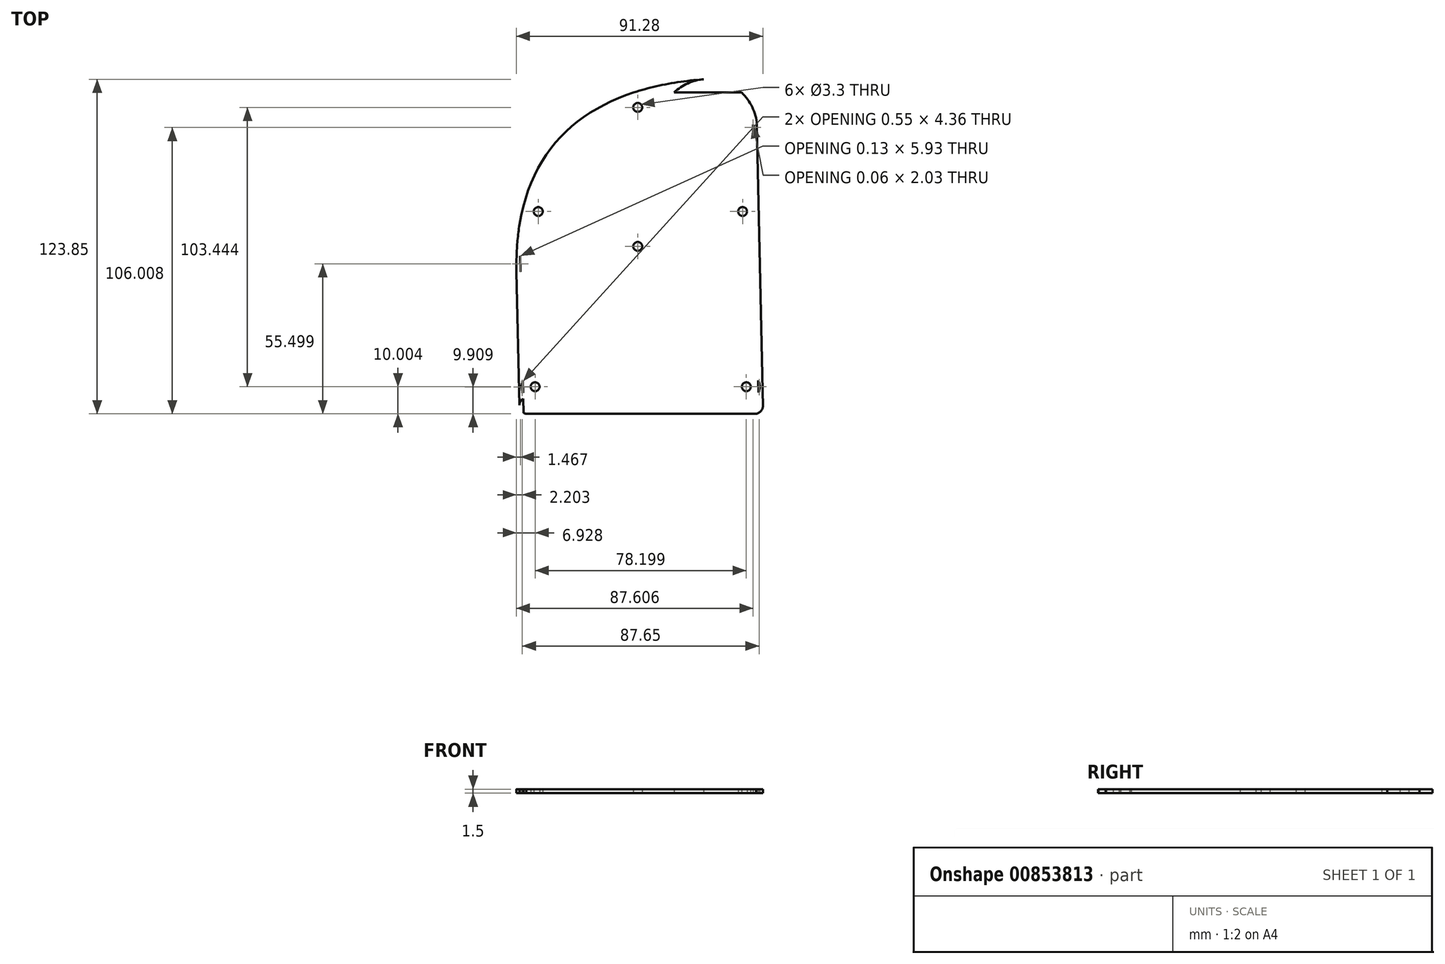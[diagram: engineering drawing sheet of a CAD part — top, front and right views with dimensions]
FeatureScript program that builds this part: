
annotation { "Feature Type Name" : "Feature", "Feature Type Description" : "" }
export const myFeature = defineFeature(function(context is Context, id is Id, definition is map)
    precondition{}
    {
        {
            var Q0;
            Q0=qCreatedBy(makeId("Top.planeOp"),FACE);
            var sketch = newSketch(context, id + "F0", { "sketchPlane" : qUnion([Q0])});
            skLineSegment(sketch, "E0.bottom", {"start": v(-43.8, -61.99) * mm, "end": v(46.4, -61.99) * mm});
            skLineSegment(sketch, "E0.top", {"start": v(-46.4, 61.99) * mm, "end": v(43.8, 61.99) * mm});
            skLineSegment(sketch, "E0.left", {"start": v(-43.8, -61.99) * mm, "end": v(-46.4, 61.99) * mm});
            skLineSegment(sketch, "E0.right", {"start": v(46.4, -61.99) * mm, "end": v(43.8, 61.99) * mm});
            skPoint(sketch, "E0.middle", {"position": v(0, 0) * mm});
            skCircle(sketch, "E1", {"center": v(25.95, 43.67) * mm, "radius": 16.76 * mm});
            skLineSegment(sketch, "E2", {"start": v(26.25, -9.49) * mm, "end": v(-11.6, 28.35) * mm, "construction": true});
            skFitSpline(sketch, "E3", {"points": [v(26.25, 61.99) * mm, v(-44.9, -9.49) * mm], "startDerivative": vector(-128.7, -8.1) * mm, "endDerivative": vector(3.04, -144.1) * mm});
            skCircle(sketch, "E4", {"center": v(43.36, -59.03) * mm, "radius": 3 * mm});
            skCircle(sketch, "E5", {"center": v(-40.86, -59.01) * mm, "radius": 3 * mm});
            skLineSegment(sketch, "E6", {"start": v(-26.25, -9.49) * mm, "end": v(-26.25, -56.26) * mm});
            skLineSegment(sketch, "E7", {"start": v(-26.25, -56.26) * mm, "end": v(-26.25, 32.47) * mm, "construction": true});
            skCircle(sketch, "E8", {"center": v(-38, -51.99) * mm, "radius": 1.65 * mm});
            skCircle(sketch, "E9", {"center": v(40.2, -51.99) * mm, "radius": 1.65 * mm});
            skCircle(sketch, "E10", {"center": v(0, 51.46) * mm, "radius": 1.65 * mm});
            skCircle(sketch, "E11", {"center": v(38.83, 12.9) * mm, "radius": 1.65 * mm});
            skCircle(sketch, "E12", {"center": v(-36.82, 12.9) * mm, "radius": 1.65 * mm});
            skLineSegment(sketch, "E13", {"start": v(-44, -51.99) * mm, "end": v(47.84, -51.99) * mm, "construction": true});
            skLineSegment(sketch, "E14", {"start": v(-42.82, 12.9) * mm, "end": v(44.83, 12.9) * mm, "construction": true});
            skPoint(sketch, "E15", {"position": v(0, 57.46) * mm});
            skCircle(sketch, "E16", {"center": v(0, 0) * mm, "radius": 1.65 * mm});
            skLineSegment(sketch, "E17.0", {"start": v(-43.8, -60.49) * mm, "end": v(46.4, -60.49) * mm});
            skFitSpline(sketch, "E18.0", {"points": [v(26.34, 60.49) * mm, v(15.73, 59.82) * mm, v(1.12, 57.15) * mm, v(-14.95, 49.87) * mm, v(-25.12, 42.49) * mm, v(-33.26, 33.05) * mm, v(-39.23, 21.43) * mm, v(-42.84, 7.46) * mm, v(-43.53, -3.53) * mm, v(-43.4, -9.45) * mm]});
            skLineSegment(sketch, "E19.0", {"start": v(-42.3, -61.95) * mm, "end": v(-44.9, 62.02) * mm});
            skLineSegment(sketch, "E20.0", {"start": v(-46.4, 56.99) * mm, "end": v(43.8, 56.99) * mm});
            skLineSegment(sketch, "E21.0", {"start": v(44.9, -62.02) * mm, "end": v(42.3, 61.95) * mm});
            skCircle(sketch, "E22", {"center": v(25.95, 43.67) * mm, "radius": 18.26 * mm});
            skCircle(sketch, "E23", {"center": v(-36.82, 12.9) * mm, "radius": 5 * mm});
            skCircle(sketch, "E24", {"center": v(38.74, 12.96) * mm, "radius": 5 * mm});
            skCircle(sketch, "E25", {"center": v(40.2, -51.99) * mm, "radius": 5 * mm});
            skCircle(sketch, "E26", {"center": v(-38, -51.99) * mm, "radius": 5 * mm});
            skCircle(sketch, "E27", {"center": v(0, 51.46) * mm, "radius": 5 * mm});
            skCircle(sketch, "E28", {"center": v(0, 0) * mm, "radius": 5 * mm});
            skPoint(sketch, "E29.endSnap0", {"position": v(1, 12.9) * mm});
            skPoint(sketch, "E30.startSnap0", {"position": v(7.33, 9.43) * mm});
            skLineSegment(sketch, "E31", {"start": v(4.22, 2.68) * mm, "end": v(33.74, 12.9) * mm});
            skLineSegment(sketch, "E32", {"start": v(-4.01, 2.98) * mm, "end": v(-31.82, 12.9) * mm});
            skLineSegment(sketch, "E33.0", {"start": v(4.55, 1.73) * mm, "end": v(34.07, 11.96) * mm});
            skLineSegment(sketch, "E34.0", {"start": v(-4.35, 2.04) * mm, "end": v(-32.16, 11.97) * mm});
            skSolve(sketch);
        }
        {
            var Q0;
            {var subQ5=sQuery(id+"F0.wireOp",EDGE,"E20.0");var subQ6=sQuery(id+"F0.wireOp",EDGE,"E3");var subQ7=makeQuery(id+"F0.imprint","INTERSECT",VERTEX,{"derivedFrom":[subQ6,subQ5]});Q0=makeQuery(id+"F0.imprint","IMPRINT",FACE,{"disambiguationData":[TD([[makeQuery(id+"F0.imprint","IMPRINT",EDGE,{"disambiguationData":[TD([[subQ7,-1.0]])],"derivedFrom":subQ6}),1.0]])]});}
            var Q1;
            Q1=makeQuery(id+"F0.imprint","IMPRINT",FACE,{"disambiguationData":[TD([[makeQuery(id+"F0.imprint","IMPRINT",EDGE,{"derivedFrom":sQuery(id+"F0.wireOp",EDGE,"E12")}),-1.0]])]});
            var Q2;
            {var subQ0=sQuery(id+"F0.wireOp",EDGE,"E23");var subQ1=sQuery(id+"F0.wireOp",EDGE,"E18.0");var subQ2=makeQuery(id+"F0.imprint","INTERSECT",VERTEX,{"disambiguationData":[OD(0.0)],"derivedFrom":[subQ1,subQ0]});Q2=makeQuery(id+"F0.imprint","IMPRINT",FACE,{"disambiguationData":[TD([[makeQuery(id+"F0.imprint","IMPRINT",EDGE,{"disambiguationData":[TD([[subQ2,-1.0]])],"derivedFrom":subQ1}),-1.0]])]});}
            var Q3;
            {var subQ0=sQuery(id+"F0.wireOp",EDGE,"TeiWms4V-cQrz-ivjK-Wwix-VJ39zWUTM9XS");Q3=makeQuery(id+"F0.imprint","IMPRINT",FACE,{"disambiguationData":[TD([[makeQuery(id+"F0.imprint","IMPRINT",EDGE,{"derivedFrom":subQ0}),-1.0]])]});}
            var Q4;
            Q4=makeQuery(id+"F0.imprint","IMPRINT",FACE,{"disambiguationData":[TD([[makeQuery(id+"F0.imprint","IMPRINT",EDGE,{"derivedFrom":sQuery(id+"F0.wireOp",EDGE,"E16")}),-1.0]])]});
            var Q5;
            {var subQ0=sQuery(id+"F0.wireOp",EDGE,"E29");Q5=makeQuery(id+"F0.imprint","IMPRINT",FACE,{"disambiguationData":[TD([[makeQuery(id+"F0.imprint","IMPRINT",EDGE,{"derivedFrom":subQ0}),1.0]])]});}
            var Q6;
            Q6=makeQuery(id+"F0.imprint","IMPRINT",FACE,{"disambiguationData":[TD([[makeQuery(id+"F0.imprint","IMPRINT",EDGE,{"derivedFrom":sQuery(id+"F0.wireOp",EDGE,"E11")}),-1.0]])]});
            var Q7;
            {var subQ0=sQuery(id+"F0.wireOp",EDGE,"E24");var subQ1=sQuery(id+"F0.wireOp",EDGE,"E21.0");var subQ2=makeQuery(id+"F0.imprint","INTERSECT",VERTEX,{"disambiguationData":[OD(0.0)],"derivedFrom":[subQ1,subQ0]});Q7=makeQuery(id+"F0.imprint","IMPRINT",FACE,{"disambiguationData":[TD([[makeQuery(id+"F0.imprint","IMPRINT",EDGE,{"disambiguationData":[TD([[subQ2,-1.0]])],"derivedFrom":subQ1}),-1.0]])]});}
            var Q8;
            {var subQ1=sQuery(id+"F0.wireOp",EDGE,"E4");var subQ5=sQuery(id+"F0.wireOp",EDGE,"E0.right");var subQ6=makeQuery(id+"F0.imprint","INTERSECT",VERTEX,{"disambiguationData":[OD(1.0)],"derivedFrom":[subQ5,subQ1]});Q8=makeQuery(id+"F0.imprint","IMPRINT",FACE,{"disambiguationData":[TD([[makeQuery(id+"F0.imprint","IMPRINT",EDGE,{"disambiguationData":[TD([[subQ6,-1.0]])],"derivedFrom":subQ5}),1.0]])]});}
            var Q9;
            {var subQ3=sQuery(id+"F0.wireOp",EDGE,"E22");var subQ7=sQuery(id+"F0.wireOp",EDGE,"E0.right");var subQ8=makeQuery(id+"F0.imprint","INTERSECT",VERTEX,{"disambiguationData":[OD(0.0)],"derivedFrom":[subQ7,subQ3]});Q9=makeQuery(id+"F0.imprint","IMPRINT",FACE,{"disambiguationData":[TD([[makeQuery(id+"F0.imprint","IMPRINT",EDGE,{"disambiguationData":[TD([[subQ8,-1.0]])],"derivedFrom":subQ7}),1.0]])]});}
            var Q10;
            {var subQ0=sQuery(id+"F0.wireOp",EDGE,"E20.0");var subQ1=sQuery(id+"F0.wireOp",EDGE,"E1");var subQ2=makeQuery(id+"F0.imprint","INTERSECT",VERTEX,{"disambiguationData":[OD(0.0)],"derivedFrom":[subQ1,subQ0]});Q10=makeQuery(id+"F0.imprint","IMPRINT",FACE,{"disambiguationData":[TD([[makeQuery(id+"F0.imprint","IMPRINT",EDGE,{"disambiguationData":[TD([[subQ2,1.0]])],"derivedFrom":subQ1}),-1.0]])]});}
            var Q11;
            {var subQ0=sQuery(id+"F0.wireOp",EDGE,"E18.0");var subQ1=sQuery(id+"F0.wireOp",EDGE,"E1");var subQ8=makeQuery(id+"F0.imprint","INTERSECT",VERTEX,{"disambiguationData":[OD(0.0)],"derivedFrom":[subQ1,subQ0]});Q11=makeQuery(id+"F0.imprint","IMPRINT",FACE,{"disambiguationData":[TD([[makeQuery(id+"F0.imprint","IMPRINT",EDGE,{"disambiguationData":[TD([[subQ8,1.0]])],"derivedFrom":subQ1}),-1.0]])]});}
            var Q12;
            {var subQ0=sQuery(id+"F0.wireOp",EDGE,"E22");var subQ1=sQuery(id+"F0.wireOp",EDGE,"E3");var subQ2=makeQuery(id+"F0.imprint","INTERSECT",VERTEX,{"disambiguationData":[OD(1.0)],"derivedFrom":[subQ1,subQ0]});Q12=makeQuery(id+"F0.imprint","IMPRINT",FACE,{"disambiguationData":[TD([[makeQuery(id+"F0.imprint","IMPRINT",EDGE,{"disambiguationData":[TD([[subQ2,-1.0]])],"derivedFrom":subQ1}),1.0]])]});}
            var Q13;
            Q13=makeQuery(id+"F0.imprint","IMPRINT",FACE,{"disambiguationData":[TD([[makeQuery(id+"F0.imprint","IMPRINT",EDGE,{"derivedFrom":sQuery(id+"F0.wireOp",EDGE,"E10")}),-1.0]])]});
            var Q14;
            {var subQ0=sQuery(id+"F0.wireOp",EDGE,"E27");var subQ1=sQuery(id+"F0.wireOp",EDGE,"E18.0");var subQ2=makeQuery(id+"F0.imprint","INTERSECT",VERTEX,{"disambiguationData":[OD(0.0)],"derivedFrom":[subQ1,subQ0]});Q14=makeQuery(id+"F0.imprint","IMPRINT",FACE,{"disambiguationData":[TD([[makeQuery(id+"F0.imprint","IMPRINT",EDGE,{"disambiguationData":[TD([[subQ2,-1.0]])],"derivedFrom":subQ1}),-1.0]])]});}
            var Q15;
            {var subQ5=sQuery(id+"F0.wireOp",EDGE,"E0.left");var subQ8=sQuery(id+"F0.wireOp",EDGE,"E3");var subQ11=makeQuery(id+"F0.imprint","INTERSECT",VERTEX,{"derivedFrom":[subQ5,subQ8]});Q15=makeQuery(id+"F0.imprint","IMPRINT",FACE,{"disambiguationData":[TD([[makeQuery(id+"F0.imprint","IMPRINT",EDGE,{"disambiguationData":[TD([[subQ11,1.0]])],"derivedFrom":subQ5}),-1.0]])]});}
            var Q16;
            Q16=makeQuery(id+"F0.imprint","IMPRINT",FACE,{"disambiguationData":[TD([[makeQuery(id+"F0.imprint","IMPRINT",EDGE,{"derivedFrom":sQuery(id+"F0.wireOp",EDGE,"E8")}),-1.0]])]});
            var Q17;
            {var subQ1=sQuery(id+"F0.wireOp",EDGE,"E5");var subQ5=sQuery(id+"F0.wireOp",EDGE,"E0.left");var subQ8=makeQuery(id+"F0.imprint","INTERSECT",VERTEX,{"disambiguationData":[OD(0.0)],"derivedFrom":[subQ5,subQ1]});Q17=makeQuery(id+"F0.imprint","IMPRINT",FACE,{"disambiguationData":[TD([[makeQuery(id+"F0.imprint","IMPRINT",EDGE,{"disambiguationData":[TD([[subQ8,-1.0]])],"derivedFrom":subQ5}),-1.0]])]});}
            var Q18;
            {var subQ0=sQuery(id+"F0.wireOp",EDGE,"E17.0");var subQ1=sQuery(id+"F0.wireOp",EDGE,"E5");var subQ2=makeQuery(id+"F0.imprint","INTERSECT",VERTEX,{"disambiguationData":[OD(0.0)],"derivedFrom":[subQ1,subQ0]});Q18=makeQuery(id+"F0.imprint","IMPRINT",FACE,{"disambiguationData":[TD([[makeQuery(id+"F0.imprint","IMPRINT",EDGE,{"disambiguationData":[TD([[subQ2,-1.0]])],"derivedFrom":subQ1}),1.0]])]});}
            var Q19;
            {var subQ1=sQuery(id+"F0.wireOp",EDGE,"E5");var subQ5=sQuery(id+"F0.wireOp",EDGE,"E0.bottom");var subQ6=makeQuery(id+"F0.imprint","INTERSECT",VERTEX,{"disambiguationData":[OD(0.0)],"derivedFrom":[subQ5,subQ1]});Q19=makeQuery(id+"F0.imprint","IMPRINT",FACE,{"disambiguationData":[TD([[makeQuery(id+"F0.imprint","IMPRINT",EDGE,{"disambiguationData":[TD([[subQ6,-1.0]])],"derivedFrom":subQ5}),1.0]])]});}
            var Q20;
            {var subQ0=sQuery(id+"F0.wireOp",EDGE,"E5");var subQ1=sQuery(id+"F0.wireOp",EDGE,"E0.bottom");var subQ2=makeQuery(id+"F0.imprint","INTERSECT",VERTEX,{"disambiguationData":[OD(1.0)],"derivedFrom":[subQ1,subQ0]});Q20=makeQuery(id+"F0.imprint","IMPRINT",FACE,{"disambiguationData":[TD([[makeQuery(id+"F0.imprint","IMPRINT",EDGE,{"disambiguationData":[TD([[subQ2,-1.0]])],"derivedFrom":subQ1}),1.0]])]});}
            var Q21;
            {var subQ0=sQuery(id+"F0.wireOp",EDGE,"E4");var subQ1=sQuery(id+"F0.wireOp",EDGE,"E0.bottom");var subQ8=makeQuery(id+"F0.imprint","INTERSECT",VERTEX,{"disambiguationData":[OD(0.0)],"derivedFrom":[subQ1,subQ0]});Q21=makeQuery(id+"F0.imprint","IMPRINT",FACE,{"disambiguationData":[TD([[makeQuery(id+"F0.imprint","IMPRINT",EDGE,{"disambiguationData":[TD([[subQ8,-1.0]])],"derivedFrom":subQ1}),1.0]])]});}
            var Q22;
            {var subQ0=sQuery(id+"F0.wireOp",EDGE,"E4");var subQ1=sQuery(id+"F0.wireOp",EDGE,"E0.right");var subQ2=makeQuery(id+"F0.imprint","INTERSECT",VERTEX,{"disambiguationData":[OD(0.0)],"derivedFrom":[subQ1,subQ0]});Q22=makeQuery(id+"F0.imprint","IMPRINT",FACE,{"disambiguationData":[TD([[makeQuery(id+"F0.imprint","IMPRINT",EDGE,{"disambiguationData":[TD([[subQ2,-1.0]])],"derivedFrom":subQ1}),1.0]])]});}
            var Q23;
            {var subQ0=sQuery(id+"F0.wireOp",EDGE,"E21.0");var subQ1=sQuery(id+"F0.wireOp",EDGE,"E4");var subQ2=makeQuery(id+"F0.imprint","INTERSECT",VERTEX,{"disambiguationData":[OD(1.0)],"derivedFrom":[subQ1,subQ0]});Q23=makeQuery(id+"F0.imprint","IMPRINT",FACE,{"disambiguationData":[TD([[makeQuery(id+"F0.imprint","IMPRINT",EDGE,{"disambiguationData":[TD([[subQ2,-1.0]])],"derivedFrom":subQ1}),1.0]])]});}
            var Q24;
            Q24=makeQuery(id+"F0.imprint","IMPRINT",FACE,{"disambiguationData":[TD([[makeQuery(id+"F0.imprint","IMPRINT",EDGE,{"derivedFrom":sQuery(id+"F0.wireOp",EDGE,"E9")}),-1.0]])]});
            var Q25;
            {var subQ1=sQuery(id+"F0.wireOp",EDGE,"E4");var subQ3=sQuery(id+"F0.wireOp",EDGE,"E21.0");var subQ5=makeQuery(id+"F0.imprint","INTERSECT",VERTEX,{"disambiguationData":[OD(0.0)],"derivedFrom":[subQ1,subQ3]});Q25=makeQuery(id+"F0.imprint","IMPRINT",FACE,{"disambiguationData":[TD([[makeQuery(id+"F0.imprint","IMPRINT",EDGE,{"disambiguationData":[TD([[subQ5,-1.0]])],"derivedFrom":subQ1}),1.0]])]});}
            var Q26;
            {var subQ0=sQuery(id+"F0.wireOp",EDGE,"E21.0");var subQ1=sQuery(id+"F0.wireOp",EDGE,"E4");var subQ2=makeQuery(id+"F0.imprint","INTERSECT",VERTEX,{"disambiguationData":[OD(0.0)],"derivedFrom":[subQ1,subQ0]});Q26=makeQuery(id+"F0.imprint","IMPRINT",FACE,{"disambiguationData":[TD([[makeQuery(id+"F0.imprint","IMPRINT",EDGE,{"disambiguationData":[TD([[subQ2,-1.0]])],"derivedFrom":subQ1}),-1.0]])]});}
            var Q27;
            {var subQ0=sQuery(id+"F0.wireOp",EDGE,"E25");var subQ1=sQuery(id+"F0.wireOp",EDGE,"E4");var subQ2=makeQuery(id+"F0.imprint","INTERSECT",VERTEX,{"disambiguationData":[OD(0.0)],"derivedFrom":[subQ1,subQ0]});Q27=makeQuery(id+"F0.imprint","IMPRINT",FACE,{"disambiguationData":[TD([[makeQuery(id+"F0.imprint","IMPRINT",EDGE,{"disambiguationData":[TD([[subQ2,-1.0]])],"derivedFrom":subQ1}),1.0]])]});}
            var Q28;
            {var subQ0=sQuery(id+"F0.wireOp",EDGE,"E25");var subQ1=sQuery(id+"F0.wireOp",EDGE,"E21.0");var subQ2=makeQuery(id+"F0.imprint","INTERSECT",VERTEX,{"disambiguationData":[OD(0.0)],"derivedFrom":[subQ1,subQ0]});Q28=makeQuery(id+"F0.imprint","IMPRINT",FACE,{"disambiguationData":[TD([[makeQuery(id+"F0.imprint","IMPRINT",EDGE,{"disambiguationData":[TD([[subQ2,-1.0]])],"derivedFrom":subQ1}),-1.0]])]});}
            var Q29;
            {var subQ0=sQuery(id+"F0.wireOp",EDGE,"E26");var subQ1=sQuery(id+"F0.wireOp",EDGE,"E19.0");var subQ2=makeQuery(id+"F0.imprint","INTERSECT",VERTEX,{"disambiguationData":[OD(0.0)],"derivedFrom":[subQ1,subQ0]});Q29=makeQuery(id+"F0.imprint","IMPRINT",FACE,{"disambiguationData":[TD([[makeQuery(id+"F0.imprint","IMPRINT",EDGE,{"disambiguationData":[TD([[subQ2,-1.0]])],"derivedFrom":subQ1}),1.0]])]});}
            var Q30;
            {var subQ0=sQuery(id+"F0.wireOp",EDGE,"E26");var subQ1=sQuery(id+"F0.wireOp",EDGE,"E5");var subQ2=makeQuery(id+"F0.imprint","INTERSECT",VERTEX,{"disambiguationData":[OD(0.0)],"derivedFrom":[subQ1,subQ0]});Q30=makeQuery(id+"F0.imprint","IMPRINT",FACE,{"disambiguationData":[TD([[makeQuery(id+"F0.imprint","IMPRINT",EDGE,{"disambiguationData":[TD([[subQ2,1.0]])],"derivedFrom":subQ1}),1.0]])]});}
            var Q31;
            {var subQ1=sQuery(id+"F0.wireOp",EDGE,"E5");var subQ5=sQuery(id+"F0.wireOp",EDGE,"E26");var subQ8=makeQuery(id+"F0.imprint","INTERSECT",VERTEX,{"disambiguationData":[OD(0.0)],"derivedFrom":[subQ1,subQ5]});Q31=makeQuery(id+"F0.imprint","IMPRINT",FACE,{"disambiguationData":[TD([[makeQuery(id+"F0.imprint","IMPRINT",EDGE,{"disambiguationData":[TD([[subQ8,-1.0]])],"derivedFrom":subQ1}),1.0]])]});}
            var Q32;
            {var subQ0=sQuery(id+"F0.wireOp",EDGE,"E26");var subQ1=sQuery(id+"F0.wireOp",EDGE,"E5");var subQ2=makeQuery(id+"F0.imprint","INTERSECT",VERTEX,{"disambiguationData":[OD(0.0)],"derivedFrom":[subQ1,subQ0]});Q32=makeQuery(id+"F0.imprint","IMPRINT",FACE,{"disambiguationData":[TD([[makeQuery(id+"F0.imprint","IMPRINT",EDGE,{"disambiguationData":[TD([[subQ2,-1.0]])],"derivedFrom":subQ1}),-1.0]])]});}
            var Q33;
            {var subQ0=sQuery(id+"F0.wireOp",EDGE,"E31");Q33=makeQuery(id+"F0.imprint","IMPRINT",FACE,{"disambiguationData":[TD([[makeQuery(id+"F0.imprint","IMPRINT",EDGE,{"derivedFrom":subQ0}),-1.0]])]});}
            var Q34;
            {var subQ0=sQuery(id+"F0.wireOp",EDGE,"E32");Q34=makeQuery(id+"F0.imprint","IMPRINT",FACE,{"disambiguationData":[TD([[makeQuery(id+"F0.imprint","IMPRINT",EDGE,{"derivedFrom":subQ0}),1.0]])]});}
            var Q35;
            {var subQ4=sQuery(id+"F0.wireOp",EDGE,"E31");Q35=makeQuery(id+"F0.imprint","IMPRINT",FACE,{"disambiguationData":[TD([[makeQuery(id+"F0.imprint","IMPRINT",EDGE,{"derivedFrom":subQ4}),1.0]])]});}
            var Q36;
            {var subQ0=sQuery(id+"F0.wireOp",EDGE,"E20.0");var subQ1=sQuery(id+"F0.wireOp",EDGE,"E1");var subQ2=makeQuery(id+"F0.imprint","INTERSECT",VERTEX,{"disambiguationData":[OD(0.0)],"derivedFrom":[subQ1,subQ0]});Q36=makeQuery(id+"F0.imprint","IMPRINT",FACE,{"disambiguationData":[TD([[makeQuery(id+"F0.imprint","IMPRINT",EDGE,{"disambiguationData":[TD([[subQ2,1.0]])],"derivedFrom":subQ1}),1.0]])]});}
            var Q37;
            {var subQ0=sQuery(id+"F0.wireOp",EDGE,"E18.0");var subQ1=sQuery(id+"F0.wireOp",EDGE,"E1");var subQ2=makeQuery(id+"F0.imprint","INTERSECT",VERTEX,{"disambiguationData":[OD(0.0)],"derivedFrom":[subQ1,subQ0]});Q37=makeQuery(id+"F0.imprint","IMPRINT",FACE,{"disambiguationData":[TD([[makeQuery(id+"F0.imprint","IMPRINT",EDGE,{"disambiguationData":[TD([[subQ2,1.0]])],"derivedFrom":subQ1}),1.0]])]});}
            var Q38;
            {var subQ0=sQuery(id+"F0.wireOp",EDGE,"E22");var subQ1=sQuery(id+"F0.wireOp",EDGE,"E18.0");var subQ2=makeQuery(id+"F0.imprint","INTERSECT",VERTEX,{"derivedFrom":[subQ1,subQ0]});Q38=makeQuery(id+"F0.imprint","IMPRINT",FACE,{"disambiguationData":[TD([[makeQuery(id+"F0.imprint","IMPRINT",EDGE,{"disambiguationData":[TD([[subQ2,-1.0]])],"derivedFrom":subQ1}),1.0]])]});}
            var Q39;
            {var subQ0=sQuery(id+"F0.wireOp",EDGE,"E18.0");var subQ1=sQuery(id+"F0.wireOp",EDGE,"E1");var subQ2=makeQuery(id+"F0.imprint","INTERSECT",VERTEX,{"disambiguationData":[OD(1.0)],"derivedFrom":[subQ1,subQ0]});Q39=makeQuery(id+"F0.imprint","IMPRINT",FACE,{"disambiguationData":[TD([[makeQuery(id+"F0.imprint","IMPRINT",EDGE,{"disambiguationData":[TD([[subQ2,-1.0]])],"derivedFrom":subQ1}),-1.0]])]});}
            var Q40;
            {var subQ0=sQuery(id+"F0.wireOp",EDGE,"E20.0");var subQ1=sQuery(id+"F0.wireOp",EDGE,"E1");var subQ2=makeQuery(id+"F0.imprint","INTERSECT",VERTEX,{"disambiguationData":[OD(1.0)],"derivedFrom":[subQ1,subQ0]});Q40=makeQuery(id+"F0.imprint","IMPRINT",FACE,{"disambiguationData":[TD([[makeQuery(id+"F0.imprint","IMPRINT",EDGE,{"disambiguationData":[TD([[subQ2,-1.0]])],"derivedFrom":subQ1}),-1.0]])]});}
            var Q41;
            {var subQ13=sQuery(id+"F0.wireOp",EDGE,"E25");var subQ14=sQuery(id+"F0.wireOp",EDGE,"E4");var subQ15=makeQuery(id+"F0.imprint","INTERSECT",VERTEX,{"disambiguationData":[OD(1.0)],"derivedFrom":[subQ14,subQ13]});Q41=makeQuery(id+"F0.imprint","IMPRINT",FACE,{"disambiguationData":[TD([[makeQuery(id+"F0.imprint","IMPRINT",EDGE,{"disambiguationData":[TD([[subQ15,-1.0]])],"derivedFrom":subQ14}),-1.0]])]});}
            extrude(context, id + "F1", {"entities" : qUnion([Q0, Q1, Q2, Q3, Q4, Q5, Q6, Q7, Q8, Q9, Q10, Q11, Q12, Q13, Q14, Q15, Q16, Q17, Q18, Q19, Q20, Q21, Q22, Q23, Q24, Q25, Q26, Q27, Q28, Q29, Q30, Q31, Q32, Q33, Q34, Q35, Q36, Q37, Q38, Q39, Q40, Q41]), "depth" : 1.5 * mm, "offsetDistance" : 25 * mm});
        }
    });
